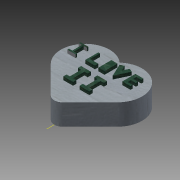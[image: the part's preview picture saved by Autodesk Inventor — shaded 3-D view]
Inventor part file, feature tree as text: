
AUTODESK INVENTOR PART (.ipt)
format: ipt  version: 2015 (Build 190159000, 159)  size: 258,048 bytes
history: native  units: mm
features: extrude x2, sketch x2, projected_geometry x1
ambient origin geometry x8: Origin, YZ Plane, XZ Plane, XY Plane, X Axis, Y Axis, Z Axis, Center Point
bodies: Volumenkörper1 (feature_tree)
feature tree (5):
  extrude  "Extrusion1"  Depth=10.0mm
  extrude  "Extrusion2"  Depth=10.0mm
  sketch  "Skizze1"  dims[d0=10.0mm d1=30.0mm d2=10.0mm]
  sketch  "Skizze2"  dims[d3=30.0mm d4=10.0mm d5=10.0mm d6=5.0mm d7=45.0deg d8=45.0deg d9=15.0mm d10=0.0mm d11=2.0mm d12=10.0mm d14=10.0mm d15=8.0mm d16=8.0mm d17=1.0mm d18=4.0mm d19=4.0mm d20=1.865658mm d21=2.0mm d22=1.0mm d23=6.0mm d24=2.0mm d26=10.0mm d27=8.726646mm d28=8.726646mm d29=5.0mm d30=8.0mm d31=8.0mm d32=9.0mm d33=9.0mm d34=8.0mm d35=6.0mm d36=5.0mm d37=2.0mm d38=2.0mm d39=90.0deg d40=2.0mm d41=2.0mm d42=2.0mm d43=7.0mm d44=2.0mm d45=0.0mm]
  projected_geometry  "Projizierte Kontur1"
